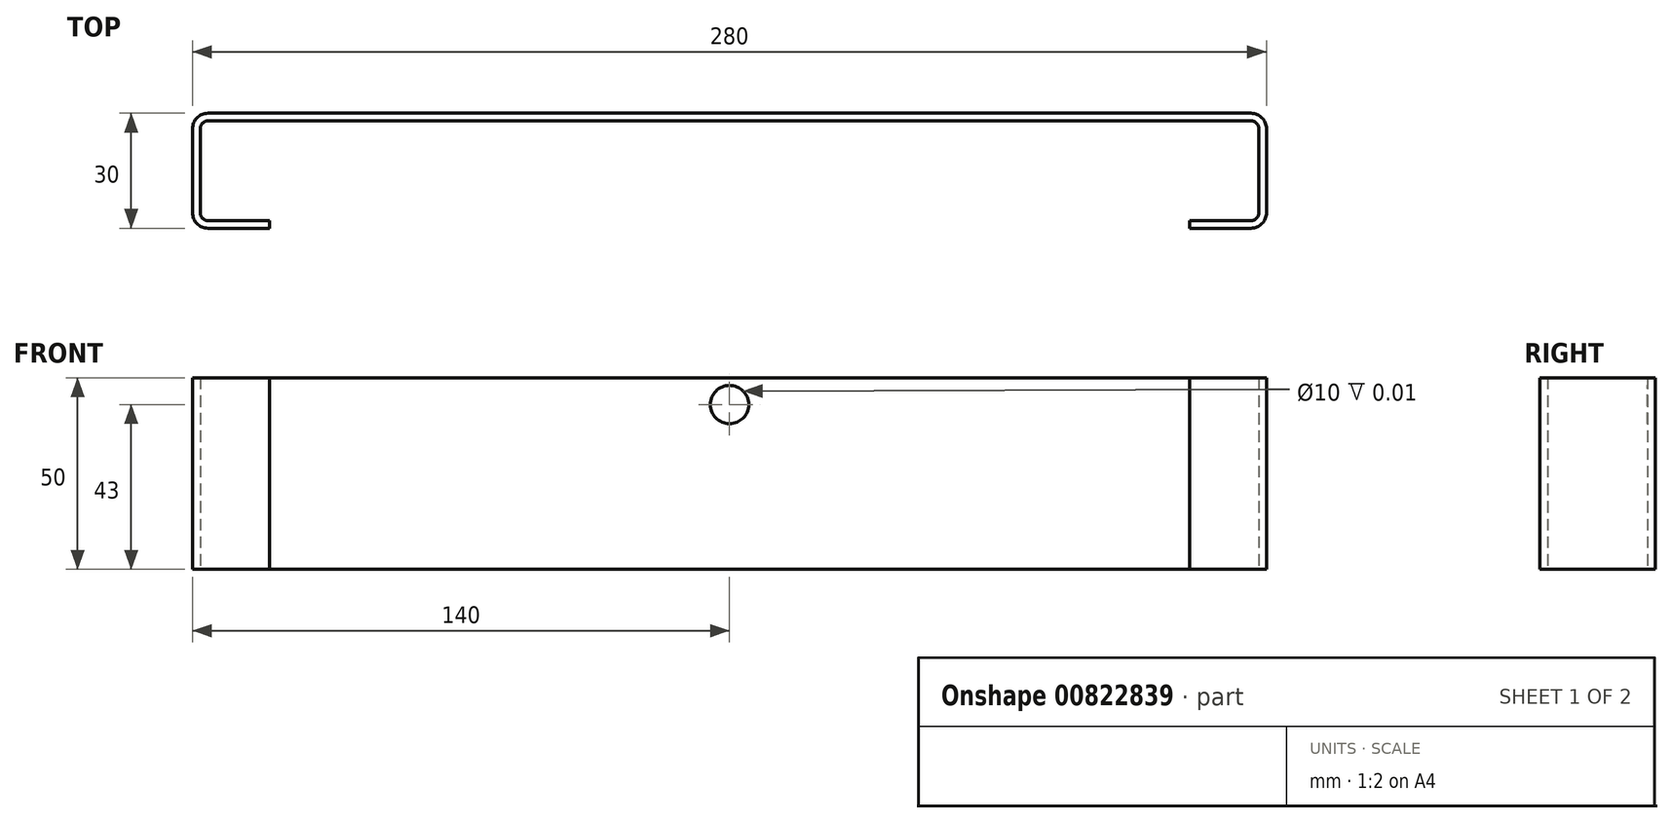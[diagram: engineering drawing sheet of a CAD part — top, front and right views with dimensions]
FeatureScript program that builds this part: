
annotation { "Feature Type Name" : "Feature", "Feature Type Description" : "" }
export const myFeature = defineFeature(function(context is Context, id is Id, definition is map)
    precondition{}
    {
        {
            var Q0;
            Q0=qCreatedBy(makeId("Top.planeOp"),FACE);
            var sketch = newSketch(context, id + "F0", { "sketchPlane" : qUnion([Q0])});
            skLineSegment(sketch, "E0", {"start": v(0, 0) * mm, "end": v(-140, 0) * mm});
            skLineSegment(sketch, "E1", {"start": v(-140, 0) * mm, "end": v(-140, -30) * mm});
            skLineSegment(sketch, "E2", {"start": v(-140, -30) * mm, "end": v(-120, -30) * mm});
            skLineSegment(sketch, "E3", {"start": v(0, 0) * mm, "end": v(0, -101.66) * mm, "construction": true});
            skLineSegment(sketch, "E4.0", {"start": v(-138, -28) * mm, "end": v(-120, -28) * mm});
            skLineSegment(sketch, "E4.1", {"start": v(-138, -2) * mm, "end": v(-138, -28) * mm});
            skLineSegment(sketch, "E4.2", {"start": v(0, -2) * mm, "end": v(-138, -2) * mm});
            skLineSegment(sketch, "E5", {"start": v(-120, -28) * mm, "end": v(-120, -30) * mm});
            skLineSegment(sketch, "E6.MirrorCS", {"start": v(120, -28) * mm, "end": v(120, -30) * mm});
            skLineSegment(sketch, "E7.MirrorCS", {"start": v(138, -2) * mm, "end": v(138, -28) * mm});
            skLineSegment(sketch, "E8.MirrorCS", {"start": v(140, 0) * mm, "end": v(140, -30) * mm});
            skLineSegment(sketch, "E9.MirrorCS", {"start": v(0, -2) * mm, "end": v(138, -2) * mm});
            skLineSegment(sketch, "E10.MirrorCS", {"start": v(138, -28) * mm, "end": v(120, -28) * mm});
            skLineSegment(sketch, "E11.MirrorCS", {"start": v(0, 0) * mm, "end": v(140, 0) * mm});
            skLineSegment(sketch, "E12.MirrorCS", {"start": v(140, -30) * mm, "end": v(120, -30) * mm});
            skSolve(sketch);
        }
        {
            var Q0;
            Q0=qSketchRegion(id+"F0",true);
            extrude(context, id + "F1", {"entities" : qUnion([Q0]), "endBound" : BoundingType.SYMMETRIC, "depth" : 50 * mm, "offsetDistance" : 25 * mm});
        }
        {
            var Q0;
            Q0=makeQuery(id+"F1.opExtrude","SWEPT_EDGE",EDGE,{"disambiguationData":[OSD([sQuery(id+"F0.wireOp",EDGE,"E4.0"),sQuery(id+"F0.wireOp",EDGE,"E4.1")])]});
            var Q1;
            Q1=makeQuery(id+"F1.opExtrude","SWEPT_EDGE",EDGE,{"disambiguationData":[OSD([sQuery(id+"F0.wireOp",EDGE,"E4.1"),sQuery(id+"F0.wireOp",EDGE,"E4.2")])]});
            var Q2;
            Q2=makeQuery(id+"F1.opExtrude","SWEPT_EDGE",EDGE,{"disambiguationData":[OSD([sQuery(id+"F0.wireOp",EDGE,"E7.MirrorCS"),sQuery(id+"F0.wireOp",EDGE,"E10.MirrorCS")])]});
            var Q3;
            Q3=makeQuery(id+"F1.opExtrude","SWEPT_EDGE",EDGE,{"disambiguationData":[OSD([sQuery(id+"F0.wireOp",EDGE,"E7.MirrorCS"),sQuery(id+"F0.wireOp",EDGE,"E9.MirrorCS")])]});
            fillet(context, id + "F2", {"entities" : qUnion([Q0, Q1, Q2, Q3]), "radius" : 2 * mm, "tangentPropagation" : true, "allowEdgeOverflow" : false});
        }
        {
            var Q0;
            Q0=makeQuery(id+"F1.opExtrude","SWEPT_EDGE",EDGE,{"disambiguationData":[OSD([sQuery(id+"F0.wireOp",EDGE,"E1"),sQuery(id+"F0.wireOp",EDGE,"E2")])]});
            var Q1;
            Q1=makeQuery(id+"F1.opExtrude","SWEPT_EDGE",EDGE,{"disambiguationData":[OSD([sQuery(id+"F0.wireOp",EDGE,"E0"),sQuery(id+"F0.wireOp",EDGE,"E1")])]});
            var Q2;
            Q2=makeQuery(id+"F1.opExtrude","SWEPT_EDGE",EDGE,{"disambiguationData":[OSD([sQuery(id+"F0.wireOp",EDGE,"E8.MirrorCS"),sQuery(id+"F0.wireOp",EDGE,"E12.MirrorCS")])]});
            var Q3;
            Q3=makeQuery(id+"F1.opExtrude","SWEPT_EDGE",EDGE,{"disambiguationData":[OSD([sQuery(id+"F0.wireOp",EDGE,"E8.MirrorCS"),sQuery(id+"F0.wireOp",EDGE,"E11.MirrorCS")])]});
            fillet(context, id + "F3", {"entities" : qUnion([Q0, Q1, Q2, Q3]), "radius" : 4 * mm, "tangentPropagation" : true, "allowEdgeOverflow" : false});
        }
        {
            var Q0;
            Q0=makeQuery(id+"F1.opExtrude","SWEPT_FACE",FACE,{"disambiguationData":[OSD([sQuery(id+"F0.wireOp",EDGE,"E4.2"),sQuery(id+"F0.wireOp",EDGE,"E9.MirrorCS")])]});
            var sketch = newSketch(context, id + "F4", { "sketchPlane" : qUnion([Q0])});
            skLineSegment(sketch, "E13.0", {"start": v(136, 25) * mm, "end": v(-136, 25) * mm, "construction": true});
            skLineSegment(sketch, "E14", {"start": v(0, 0) * mm, "end": v(0, 18) * mm, "construction": true});
            skCircle(sketch, "E15", {"center": v(0, 18) * mm, "radius": 5 * mm});
            skSolve(sketch);
        }
        {
            var Q0;
            Q0 = qSketchRegion(id + "F4", true);
            extrude(context, id + "F5", {"entities" : qUnion([Q0]), "operationType" : NewBodyOperationType.REMOVE, "oppositeDirection" : true, "depth" : 0.01 * mm, "offsetDistance" : 25 * mm});
        }
    });
